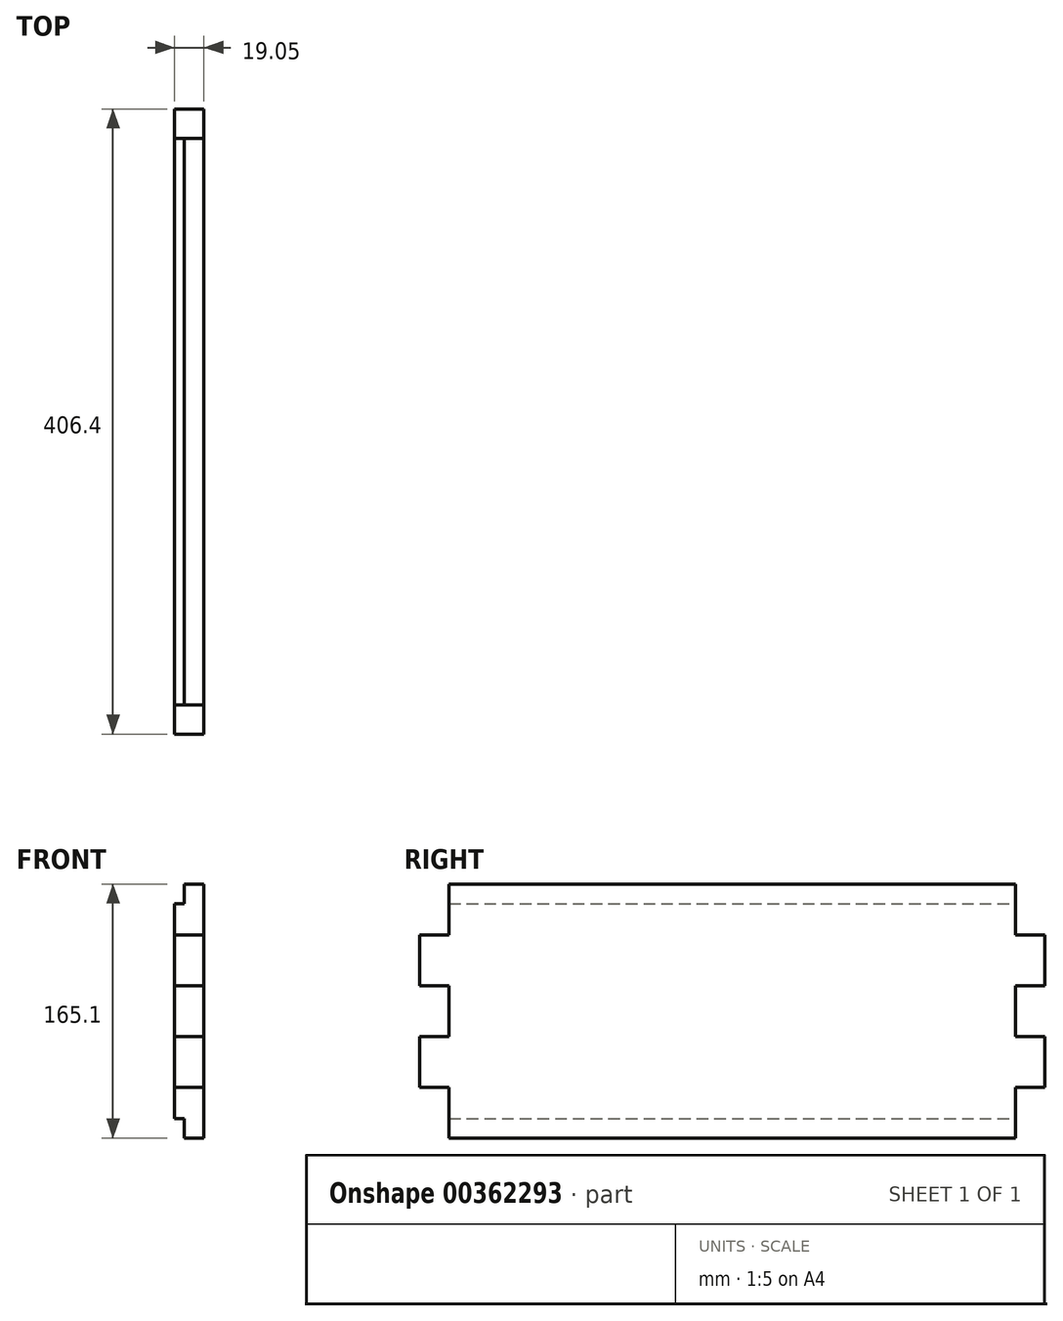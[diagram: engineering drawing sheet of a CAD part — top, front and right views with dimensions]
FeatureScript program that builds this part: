
annotation { "Feature Type Name" : "Feature", "Feature Type Description" : "" }
export const myFeature = defineFeature(function(context is Context, id is Id, definition is map)
    precondition{}
    {
        {
            var Q0;
            Q0=qCreatedBy(makeId("Right.planeOp"),FACE);
            var sketch = newSketch(context, id + "F0", { "sketchPlane" : qUnion([Q0])});
            skLineSegment(sketch, "E0.bottom", {"start": v(-208.99, 107.95) * mm, "end": v(159.31, 107.95) * mm});
            skLineSegment(sketch, "E0.top", {"start": v(-208.99, -57.15) * mm, "end": v(159.31, -57.15) * mm});
            skLineSegment(sketch, "E0.left", {"start": v(-208.99, 107.95) * mm, "end": v(-208.99, -57.15) * mm});
            skLineSegment(sketch, "E0.right", {"start": v(159.31, 107.95) * mm, "end": v(159.31, -57.15) * mm});
            skLineSegment(sketch, "E1", {"start": v(-208.99, 74.93) * mm, "end": v(-228.04, 74.93) * mm});
            skLineSegment(sketch, "E2", {"start": v(-208.99, 41.91) * mm, "end": v(-228.04, 41.91) * mm});
            skLineSegment(sketch, "E3", {"start": v(-228.04, 41.91) * mm, "end": v(-228.04, 74.93) * mm});
            skLineSegment(sketch, "E4", {"start": v(-208.99, 8.9) * mm, "end": v(-228.04, 8.9) * mm});
            skLineSegment(sketch, "E5", {"start": v(-208.99, -24.13) * mm, "end": v(-228.04, -24.13) * mm});
            skLineSegment(sketch, "E6", {"start": v(-228.04, -24.13) * mm, "end": v(-228.04, 8.9) * mm});
            skLineSegment(sketch, "E7", {"start": v(159.31, 74.93) * mm, "end": v(178.36, 74.93) * mm});
            skLineSegment(sketch, "E8", {"start": v(159.31, 41.91) * mm, "end": v(178.36, 41.91) * mm});
            skLineSegment(sketch, "E9", {"start": v(178.36, 41.91) * mm, "end": v(178.36, 74.93) * mm});
            skLineSegment(sketch, "E10", {"start": v(159.31, 8.9) * mm, "end": v(178.36, 8.9) * mm});
            skLineSegment(sketch, "E11", {"start": v(178.36, 8.9) * mm, "end": v(178.36, -24.13) * mm});
            skLineSegment(sketch, "E12", {"start": v(178.36, -24.13) * mm, "end": v(159.31, -24.13) * mm});
            skLineSegment(sketch, "E13", {"start": v(-208.99, 95.25) * mm, "end": v(159.31, 95.25) * mm});
            skLineSegment(sketch, "E14", {"start": v(-208.99, -44.45) * mm, "end": v(159.31, -44.45) * mm});
            skSolve(sketch);
        }
        {
            var Q0;
            Q0 = qSketchRegion(id + "F0", true);
            extrude(context, id + "F1", {"entities" : qUnion([Q0]), "depth" : 19.05 * mm});
        }
        {
            var Q0;
            {var subQ0=sQuery(id+"F0.wireOp",EDGE,"E0.bottom");Q0=makeQuery(id+"F0.imprint","IMPRINT",FACE,{"disambiguationData":[TD([[makeQuery(id+"F0.imprint","IMPRINT",EDGE,{"derivedFrom":subQ0}),-1.0]])]});}
            extrude(context, id + "F2", {"entities" : qUnion([Q0]), "operationType" : NewBodyOperationType.REMOVE, "depth" : 6.35 * mm});
        }
        {
            var Q0;
            {var subQ0=sQuery(id+"F0.wireOp",EDGE,"E0.top");Q0=makeQuery(id+"F0.imprint","IMPRINT",FACE,{"disambiguationData":[TD([[makeQuery(id+"F0.imprint","IMPRINT",EDGE,{"derivedFrom":subQ0}),1.0]])]});}
            extrude(context, id + "F3", {"entities" : qUnion([Q0]), "operationType" : NewBodyOperationType.REMOVE, "depth" : 6.35 * mm});
        }
    });
